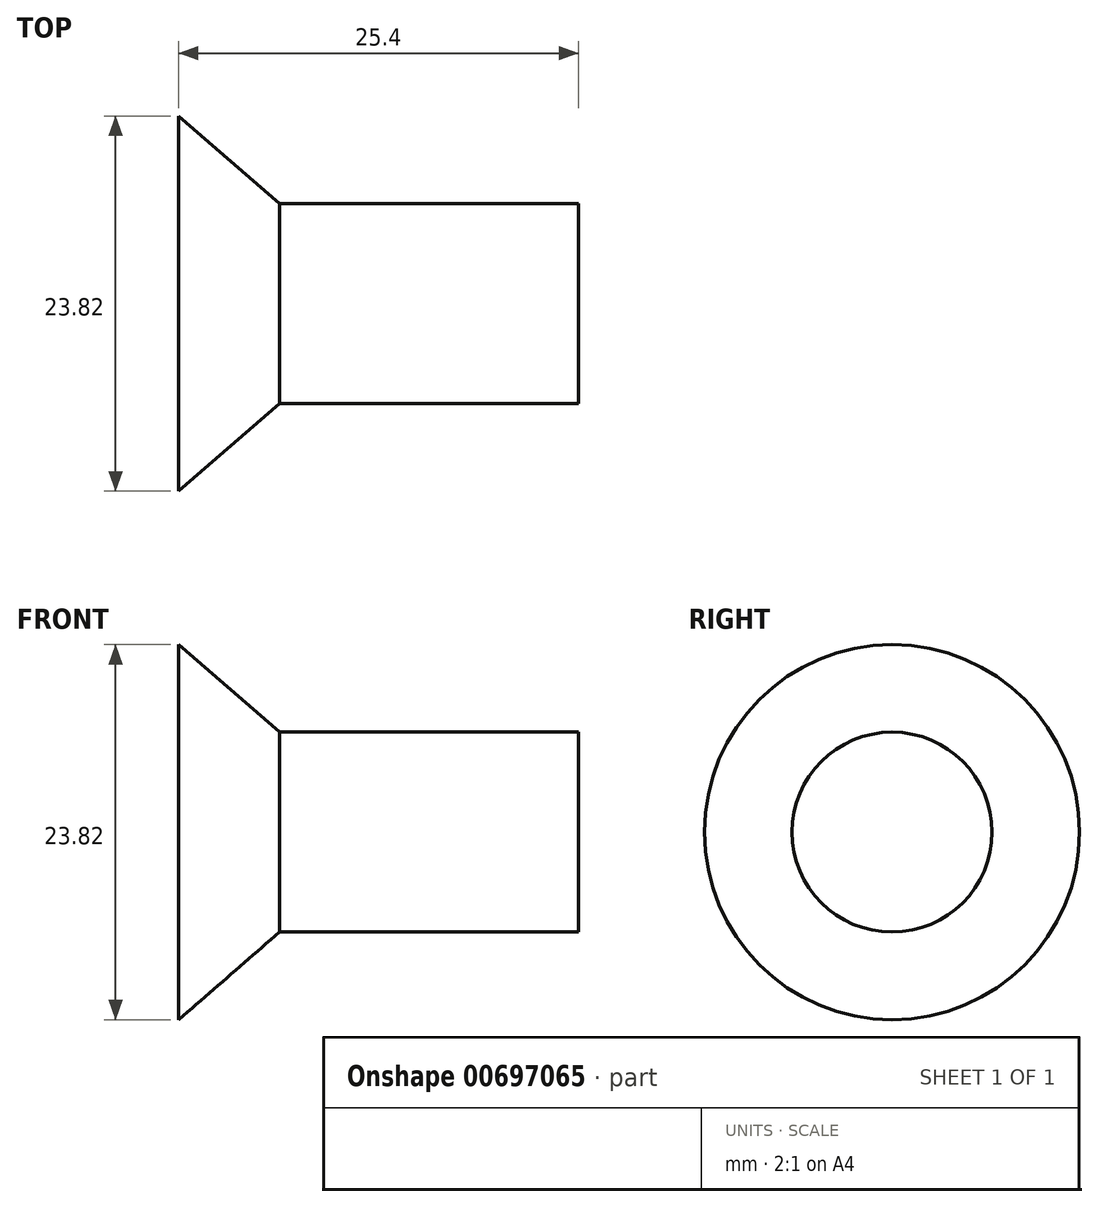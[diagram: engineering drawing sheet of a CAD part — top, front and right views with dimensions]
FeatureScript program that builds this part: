
annotation { "Feature Type Name" : "Feature", "Feature Type Description" : "" }
export const myFeature = defineFeature(function(context is Context, id is Id, definition is map)
    precondition{}
    {
        {
            var Q0;
            Q0=qCreatedBy(makeId("Front.planeOp"),FACE);
            var sketch = newSketch(context, id + "F0", { "sketchPlane" : qUnion([Q0])});
            skLineSegment(sketch, "E0", {"start": v(137.07, 0) * mm, "end": v(-144.26, 0) * mm, "construction": true});
            skLineSegment(sketch, "E1", {"start": v(-22.06, 0) * mm, "end": v(-22.06, 11.91) * mm});
            skLineSegment(sketch, "E2", {"start": v(-22.06, 11.91) * mm, "end": v(-15.66, 6.35) * mm});
            skLineSegment(sketch, "E3", {"start": v(-15.66, 6.35) * mm, "end": v(3.34, 6.35) * mm});
            skLineSegment(sketch, "E4", {"start": v(3.34, 6.35) * mm, "end": v(3.34, 0) * mm});
            skLineSegment(sketch, "E5", {"start": v(3.34, 0) * mm, "end": v(-22.06, 0) * mm});
            skSolve(sketch);
        }
        {
            var Q0;
            Q0 = qSketchRegion(id + "F0", true);
            var Q1;
            Q1=sQuery(id+"F0.wireOp",EDGE,"E0");
            revolve(context, id + "F1", {"entities" : qUnion([Q0]), "axis" : qUnion([Q1]), "revolveType" : RevolveType.FULL});
        }
    });
